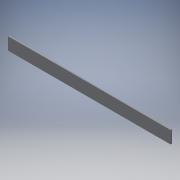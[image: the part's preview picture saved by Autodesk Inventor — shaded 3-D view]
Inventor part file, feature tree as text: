
AUTODESK INVENTOR PART (.ipt)
format: ipt  version: 2018 (Build 220112000, 112)  size: 92,160 bytes
history: native  units: in
note: dims shown in document units (in); Inventor stores cm internally (conversion verified against a paired STEP export)
features: extrude x1, sketch x1
ambient origin geometry x8: Origin, YZ Plane, XZ Plane, XY Plane, X Axis, Y Axis, Z Axis, Center Point
bodies: Solid1 (feature_tree)
feature tree (2):
  extrude  "Extrusion1"  Depth=1.0in
  sketch  "Sketch1"  dims[d2=14.5in d3=1.0in d4=0.1in d5=0.0in]
